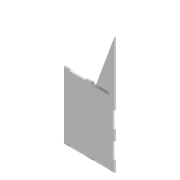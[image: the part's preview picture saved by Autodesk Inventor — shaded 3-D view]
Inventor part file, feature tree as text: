
AUTODESK INVENTOR PART (.ipt)
format: ipt  version: 2022 (Build 260153000, 153)  size: 122,880 bytes
history: native  units: mm
features: other x3, extrude x2, sketch x2, reference x1
ambient origin geometry x8: Origin, YZ Plane, XZ Plane, XY Plane, X Axis, Y Axis, Z Axis, Center Point
bodies: Solid1 (feature_tree)
feature tree (8):
  extrude  "Extrusion1"  Depth=5.0mm
  extrude  "Extrusion2"  Depth=5.0mm
  sketch  "Sketch1"  dims[d0=50.0mm d1=5.0mm]
  reference  "Reference1"
  sketch  "Sketch2"  dims[d2=50.0mm d3=5.0mm d4=20.0mm d5=15.0mm d6=50.0mm d7=5.0mm d8=5.0mm d9=15.0mm d10=5.0mm d11=0.0mm d12=5.0mm d13=50.0mm d14=5.0mm d15=50.0mm d16=30.0mm d17=30.0mm d18=5.0mm d19=0.0mm]
  parser-record x1  (decoder bookkeeping rows leaked as tree rows — omitted from the tree; the rows remain in map.json)
  other  "Ensamble caja.iam"
  other  "Modelo base:1"
note: 1 file-system path scrubbed to <path> (originals preserved in map.json)
